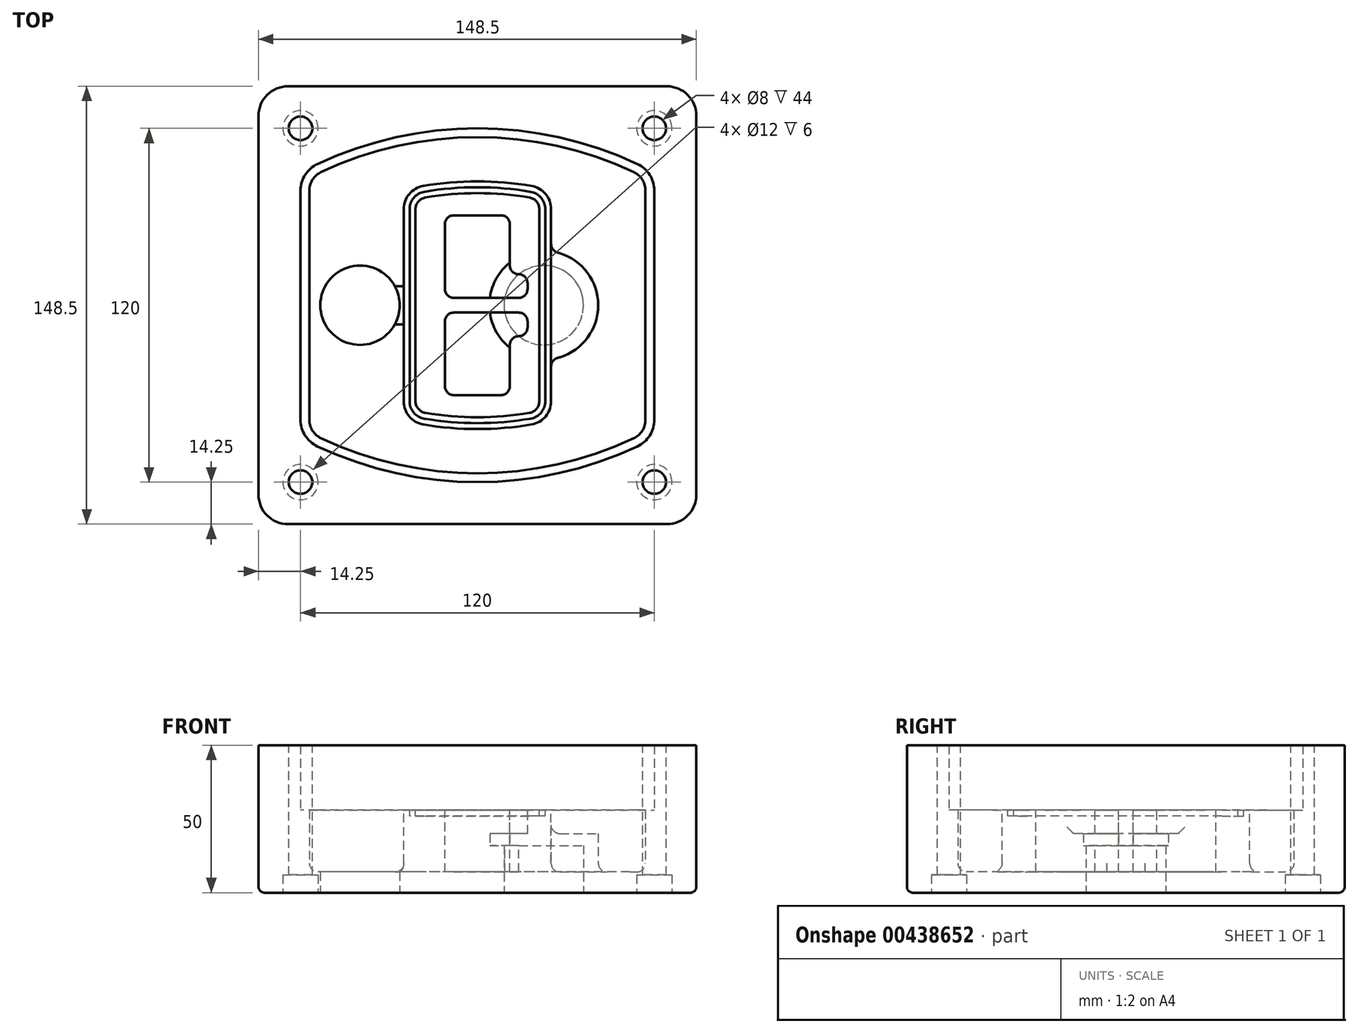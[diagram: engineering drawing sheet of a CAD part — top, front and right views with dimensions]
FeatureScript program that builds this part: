
annotation { "Feature Type Name" : "Feature", "Feature Type Description" : "" }
export const myFeature = defineFeature(function(context is Context, id is Id, definition is map)
    precondition{}
    {
        {
            var Q0;
            Q0=qCreatedBy(makeId("Top.planeOp"),FACE);
            var sketch = newSketch(context, id + "F0", { "sketchPlane" : qUnion([Q0])});
            skPoint(sketch, "E0.rect.middle", {"position": v(0, 0) * mm});
            skLineSegment(sketch, "E1.bottom", {"start": v(-64.25, -74.25) * mm, "end": v(64.25, -74.25) * mm});
            skLineSegment(sketch, "E1.top", {"start": v(-64.25, 74.25) * mm, "end": v(64.25, 74.25) * mm});
            skLineSegment(sketch, "E1.left", {"start": v(-74.25, -64.25) * mm, "end": v(-74.25, 64.25) * mm});
            skLineSegment(sketch, "E1.right", {"start": v(74.25, -64.25) * mm, "end": v(74.25, 64.25) * mm});
            skLineSegment(sketch, "E2", {"start": v(-74.25, 74.25) * mm, "end": v(74.25, -74.25) * mm, "construction": true});
            skLineSegment(sketch, "E3", {"start": v(74.25, 74.25) * mm, "end": v(-74.25, -74.25) * mm, "construction": true});
            skCircle(sketch, "E4", {"center": v(-60, 60) * mm, "radius": 4 * mm});
            skCircle(sketch, "E5", {"center": v(60, 60) * mm, "radius": 4 * mm});
            skCircle(sketch, "E6", {"center": v(60, -60) * mm, "radius": 4 * mm});
            skCircle(sketch, "E7", {"center": v(-60, -60) * mm, "radius": 4 * mm});
            skLineSegment(sketch, "E8", {"start": v(-60, 60) * mm, "end": v(60, 60) * mm, "construction": true});
            skLineSegment(sketch, "E9", {"start": v(60, 60) * mm, "end": v(60, -60) * mm, "construction": true});
            skLineSegment(sketch, "E10", {"start": v(60, -60) * mm, "end": v(-60, -60) * mm, "construction": true});
            skLineSegment(sketch, "E11", {"start": v(-60, -60) * mm, "end": v(-60, 60) * mm, "construction": true});
            skLineSegment(sketch, "E12", {"start": v(-60, 38.83) * mm, "end": v(-60, -38.83) * mm});
            skLineSegment(sketch, "E13", {"start": v(60, 38.83) * mm, "end": v(60, -38.83) * mm});
            skArc(sketch, "E14", {"start": v(54.26, 47.88) * mm, "mid": v(0, 60) * mm, "end": v(-54.26, 47.88) * mm});
            skArc(sketch, "E15", {"start": v(-54.26, -47.88) * mm, "mid": v(0, -60) * mm, "end": v(54.26, -47.88) * mm});
            skLineSegment(sketch, "E16", {"start": v(-60, 0) * mm, "end": v(60, 0) * mm, "construction": true});
            skPoint(sketch, "E17.visualSharp", {"position": v(-60, -45) * mm});
            skArc(sketch, "E17.filletArc", {"start": v(-60, -38.83) * mm, "mid": v(-58.44, -44.2) * mm, "end": v(-54.26, -47.88) * mm});
            skPoint(sketch, "E18.visualSharp", {"position": v(-60, 45) * mm});
            skArc(sketch, "E18.filletArc", {"start": v(-54.26, 47.88) * mm, "mid": v(-58.44, 44.2) * mm, "end": v(-60, 38.83) * mm});
            skPoint(sketch, "E19.visualSharp", {"position": v(60, 45) * mm});
            skArc(sketch, "E19.filletArc", {"start": v(60, 38.83) * mm, "mid": v(58.44, 44.2) * mm, "end": v(54.26, 47.88) * mm});
            skPoint(sketch, "E20.visualSharp", {"position": v(60, -45) * mm});
            skArc(sketch, "E20.filletArc", {"start": v(54.26, -47.88) * mm, "mid": v(58.44, -44.2) * mm, "end": v(60, -38.83) * mm});
            skPoint(sketch, "E21.visualSharp", {"position": v(-74.25, 74.25) * mm});
            skArc(sketch, "E21.filletArc", {"start": v(-64.25, 74.25) * mm, "mid": v(-71.32, 71.32) * mm, "end": v(-74.25, 64.25) * mm});
            skPoint(sketch, "E22.visualSharp", {"position": v(74.25, 74.25) * mm});
            skArc(sketch, "E22.filletArc", {"start": v(74.25, 64.25) * mm, "mid": v(71.32, 71.32) * mm, "end": v(64.25, 74.25) * mm});
            skPoint(sketch, "E23.visualSharp", {"position": v(74.25, -74.25) * mm});
            skArc(sketch, "E23.filletArc", {"start": v(64.25, -74.25) * mm, "mid": v(71.32, -71.32) * mm, "end": v(74.25, -64.25) * mm});
            skPoint(sketch, "E24.visualSharp", {"position": v(-74.25, -74.25) * mm});
            skArc(sketch, "E24.filletArc", {"start": v(-74.25, -64.25) * mm, "mid": v(-71.32, -71.32) * mm, "end": v(-64.25, -74.25) * mm});
            skArc(sketch, "E25.0", {"start": v(57, 38.83) * mm, "mid": v(55.9, 42.58) * mm, "end": v(52.98, 45.17) * mm});
            skLineSegment(sketch, "E25.1", {"start": v(57, 38.83) * mm, "end": v(57, -38.83) * mm});
            skArc(sketch, "E25.2", {"start": v(52.98, -45.17) * mm, "mid": v(55.9, -42.58) * mm, "end": v(57, -38.83) * mm});
            skArc(sketch, "E25.3", {"start": v(-52.98, -45.17) * mm, "mid": v(0, -57) * mm, "end": v(52.98, -45.17) * mm});
            skArc(sketch, "E25.4", {"start": v(-57, -38.83) * mm, "mid": v(-55.9, -42.58) * mm, "end": v(-52.98, -45.17) * mm});
            skArc(sketch, "E25.5", {"start": v(52.98, 45.17) * mm, "mid": v(0, 57) * mm, "end": v(-52.98, 45.17) * mm});
            skLineSegment(sketch, "E25.6", {"start": v(-57, 38.83) * mm, "end": v(-57, -38.83) * mm});
            skArc(sketch, "E25.7", {"start": v(-52.98, 45.17) * mm, "mid": v(-55.9, 42.58) * mm, "end": v(-57, 38.83) * mm});
            skArc(sketch, "E26.0", {"start": v(-55.96, 51.5) * mm, "mid": v(-61.82, 46.33) * mm, "end": v(-64, 38.83) * mm});
            skArc(sketch, "E26.1", {"start": v(55.96, 51.5) * mm, "mid": v(0, 64) * mm, "end": v(-55.96, 51.5) * mm});
            skArc(sketch, "E26.2", {"start": v(64, 38.83) * mm, "mid": v(61.82, 46.33) * mm, "end": v(55.96, 51.5) * mm});
            skLineSegment(sketch, "E26.3", {"start": v(64, 38.83) * mm, "end": v(64, -38.83) * mm});
            skArc(sketch, "E26.4", {"start": v(55.96, -51.5) * mm, "mid": v(61.82, -46.33) * mm, "end": v(64, -38.83) * mm});
            skLineSegment(sketch, "E26.5", {"start": v(-64, 38.83) * mm, "end": v(-64, -38.83) * mm});
            skArc(sketch, "E26.6", {"start": v(-55.96, -51.5) * mm, "mid": v(0, -64) * mm, "end": v(55.96, -51.5) * mm});
            skArc(sketch, "E26.7", {"start": v(-64, -38.83) * mm, "mid": v(-61.82, -46.33) * mm, "end": v(-55.96, -51.5) * mm});
            skSolve(sketch);
        }
        {
            var Q0;
            Q0=makeQuery(id+"F0.imprint","IMPRINT",FACE,{"disambiguationData":[TD([[makeQuery(id+"F0.imprint","IMPRINT",EDGE,{"derivedFrom":sQuery(id+"F0.wireOp",EDGE,"E1.bottom")}),1.0]])]});
            var Q1;
            Q1=makeQuery(id+"F0.imprint","IMPRINT",FACE,{"disambiguationData":[TD([[makeQuery(id+"F0.imprint","IMPRINT",EDGE,{"derivedFrom":sQuery(id+"F0.wireOp",EDGE,"E12")}),1.0]])]});
            var Q2;
            Q2=makeQuery(id+"F0.imprint","IMPRINT",FACE,{"disambiguationData":[TD([[makeQuery(id+"F0.imprint","IMPRINT",EDGE,{"derivedFrom":sQuery(id+"F0.wireOp",EDGE,"E25.0")}),1.0]])]});
            var Q3;
            Q3=makeQuery(id+"F0.imprint","IMPRINT",FACE,{"disambiguationData":[TD([[makeQuery(id+"F0.imprint","IMPRINT",EDGE,{"derivedFrom":sQuery(id+"F0.wireOp",EDGE,"E12")}),-1.0]])]});
            extrude(context, id + "F1", {"entities" : qUnion([Q0, Q1, Q2, Q3]), "oppositeDirection" : true, "depth" : 25 * mm});
        }
        {
            var Q0;
            Q0=makeQuery(id+"F0.imprint","IMPRINT",FACE,{"disambiguationData":[TD([[makeQuery(id+"F0.imprint","IMPRINT",EDGE,{"derivedFrom":sQuery(id+"F0.wireOp",EDGE,"E12")}),1.0]])]});
            extrude(context, id + "F2", {"entities" : qUnion([Q0]), "operationType" : NewBodyOperationType.ADD, "depth" : 3 * mm});
        }
        {
            var Q0;
            Q0=makeQuery(id+"F0.imprint","IMPRINT",FACE,{"disambiguationData":[TD([[makeQuery(id+"F0.imprint","IMPRINT",EDGE,{"derivedFrom":sQuery(id+"F0.wireOp",EDGE,"E25.0")}),1.0]])]});
            extrude(context, id + "F3", {"entities" : qUnion([Q0]), "operationType" : NewBodyOperationType.REMOVE, "oppositeDirection" : true, "depth" : 18 * mm});
        }
        {
            var Q0;
            Q0=makeQuery(id+"F2.opExtrude","CAP_FACE",FACE,{"disambiguationData":[OSD([sQuery(id+"F0.wireOp",EDGE,"E12"),sQuery(id+"F0.wireOp",EDGE,"E13"),sQuery(id+"F0.wireOp",EDGE,"E14"),sQuery(id+"F0.wireOp",EDGE,"E15"),sQuery(id+"F0.wireOp",EDGE,"E17.filletArc"),sQuery(id+"F0.wireOp",EDGE,"E18.filletArc"),sQuery(id+"F0.wireOp",EDGE,"E19.filletArc"),sQuery(id+"F0.wireOp",EDGE,"E20.filletArc"),sQuery(id+"F0.wireOp",EDGE,"E25.0"),sQuery(id+"F0.wireOp",EDGE,"E25.1"),sQuery(id+"F0.wireOp",EDGE,"E25.2"),sQuery(id+"F0.wireOp",EDGE,"E25.3"),sQuery(id+"F0.wireOp",EDGE,"E25.4"),sQuery(id+"F0.wireOp",EDGE,"E25.5"),sQuery(id+"F0.wireOp",EDGE,"E25.6"),sQuery(id+"F0.wireOp",EDGE,"E25.7")])],"isStart":false});
            var sketch = newSketch(context, id + "F4", { "sketchPlane" : qUnion([Q0])});
            skArc(sketch, "E27.0", {"start": v(-18.34, -40.45) * mm, "mid": v(0, -42) * mm, "end": v(18.34, -40.45) * mm});
            skArc(sketch, "E28.0", {"start": v(18.34, 40.45) * mm, "mid": v(0, 42) * mm, "end": v(-18.34, 40.45) * mm});
            skLineSegment(sketch, "E29", {"start": v(-25, 32.57) * mm, "end": v(-25, -32.57) * mm});
            skLineSegment(sketch, "E30", {"start": v(25, 32.57) * mm, "end": v(25, -32.57) * mm});
            skLineSegment(sketch, "E31", {"start": v(-25, 39.1) * mm, "end": v(25, 39.1) * mm, "construction": true});
            skLineSegment(sketch, "E32", {"start": v(-25, -39.1) * mm, "end": v(25, -39.1) * mm, "construction": true});
            skPoint(sketch, "E33.visualSharp", {"position": v(-25, 39.1) * mm});
            skArc(sketch, "E33.filletArc", {"start": v(-18.34, 40.45) * mm, "mid": v(-23.11, 37.73) * mm, "end": v(-25, 32.57) * mm});
            skPoint(sketch, "E34.visualSharp", {"position": v(25, 39.1) * mm});
            skArc(sketch, "E34.filletArc", {"start": v(25, 32.57) * mm, "mid": v(23.11, 37.73) * mm, "end": v(18.34, 40.45) * mm});
            skPoint(sketch, "E35.visualSharp", {"position": v(25, -39.1) * mm});
            skArc(sketch, "E35.filletArc", {"start": v(18.34, -40.45) * mm, "mid": v(23.11, -37.73) * mm, "end": v(25, -32.57) * mm});
            skPoint(sketch, "E36.visualSharp", {"position": v(-25, -39.1) * mm});
            skArc(sketch, "E36.filletArc", {"start": v(-25, -32.57) * mm, "mid": v(-23.11, -37.73) * mm, "end": v(-18.34, -40.45) * mm});
            skArc(sketch, "E37.0", {"start": v(52.98, 45.17) * mm, "mid": v(0, 57) * mm, "end": v(-52.98, 45.17) * mm});
            skArc(sketch, "E37.1", {"start": v(-52.98, 45.17) * mm, "mid": v(-55.9, 42.58) * mm, "end": v(-57, 38.83) * mm});
            skLineSegment(sketch, "E37.2", {"start": v(-57, 38.83) * mm, "end": v(-57, -38.83) * mm});
            skArc(sketch, "E37.3", {"start": v(-57, -38.83) * mm, "mid": v(-55.9, -42.58) * mm, "end": v(-52.98, -45.17) * mm});
            skArc(sketch, "E37.4", {"start": v(-52.98, -45.17) * mm, "mid": v(0, -57) * mm, "end": v(52.98, -45.17) * mm});
            skArc(sketch, "E37.5", {"start": v(52.98, -45.17) * mm, "mid": v(55.9, -42.58) * mm, "end": v(57, -38.83) * mm});
            skLineSegment(sketch, "E37.6", {"start": v(57, 38.83) * mm, "end": v(57, -38.83) * mm});
            skArc(sketch, "E37.7", {"start": v(57, 38.83) * mm, "mid": v(55.9, 42.58) * mm, "end": v(52.98, 45.17) * mm});
            skLineSegment(sketch, "E38.0", {"start": v(23, 32.57) * mm, "end": v(23, -32.57) * mm});
            skArc(sketch, "E38.1", {"start": v(18, -38.48) * mm, "mid": v(21.58, -36.44) * mm, "end": v(23, -32.57) * mm});
            skArc(sketch, "E38.2", {"start": v(-18, -38.48) * mm, "mid": v(0, -40) * mm, "end": v(18, -38.48) * mm});
            skArc(sketch, "E38.3", {"start": v(-23, -32.57) * mm, "mid": v(-21.58, -36.44) * mm, "end": v(-18, -38.48) * mm});
            skLineSegment(sketch, "E38.4", {"start": v(-23, 32.57) * mm, "end": v(-23, -32.57) * mm});
            skArc(sketch, "E38.5", {"start": v(23, 32.57) * mm, "mid": v(21.58, 36.44) * mm, "end": v(18, 38.48) * mm});
            skArc(sketch, "E38.6", {"start": v(-18, 38.48) * mm, "mid": v(-21.58, 36.44) * mm, "end": v(-23, 32.57) * mm});
            skArc(sketch, "E38.7", {"start": v(18, 38.48) * mm, "mid": v(0, 40) * mm, "end": v(-18, 38.48) * mm});
            skArc(sketch, "E39.0", {"start": v(21, 32.57) * mm, "mid": v(20.06, 35.15) * mm, "end": v(17.67, 36.5) * mm});
            skLineSegment(sketch, "E39.1", {"start": v(21, 32.57) * mm, "end": v(21, -32.57) * mm});
            skArc(sketch, "E39.2", {"start": v(17.67, -36.5) * mm, "mid": v(20.06, -35.15) * mm, "end": v(21, -32.57) * mm});
            skArc(sketch, "E39.3", {"start": v(-17.67, -36.5) * mm, "mid": v(0, -38) * mm, "end": v(17.67, -36.5) * mm});
            skArc(sketch, "E39.4", {"start": v(-21, -32.57) * mm, "mid": v(-20.06, -35.15) * mm, "end": v(-17.67, -36.5) * mm});
            skArc(sketch, "E39.5", {"start": v(17.67, 36.5) * mm, "mid": v(0, 38) * mm, "end": v(-17.67, 36.5) * mm});
            skLineSegment(sketch, "E39.6", {"start": v(-21, 32.57) * mm, "end": v(-21, -32.57) * mm});
            skArc(sketch, "E39.7", {"start": v(-17.67, 36.5) * mm, "mid": v(-20.06, 35.15) * mm, "end": v(-21, 32.57) * mm});
            skLineSegment(sketch, "E40", {"start": v(-25, 0) * mm, "end": v(25, 0) * mm, "construction": true});
            skLineSegment(sketch, "E41", {"start": v(-11, 5.5) * mm, "end": v(-11, 27.5) * mm});
            skLineSegment(sketch, "E42", {"start": v(-8, 30.5) * mm, "end": v(8, 30.5) * mm});
            skLineSegment(sketch, "E43", {"start": v(11, 27.5) * mm, "end": v(11, 13.5) * mm});
            skLineSegment(sketch, "E44", {"start": v(14, 10.5) * mm, "end": v(14, 10.5) * mm});
            skLineSegment(sketch, "E45", {"start": v(17, 7.5) * mm, "end": v(17, 5.5) * mm});
            skLineSegment(sketch, "E46", {"start": v(14, 2.5) * mm, "end": v(-8, 2.5) * mm});
            skPoint(sketch, "E47.visualSharp", {"position": v(-11, 30.5) * mm});
            skArc(sketch, "E47.filletArc", {"start": v(-8, 30.5) * mm, "mid": v(-10.12, 29.62) * mm, "end": v(-11, 27.5) * mm});
            skPoint(sketch, "E48.visualSharp", {"position": v(11, 30.5) * mm});
            skArc(sketch, "E48.filletArc", {"start": v(11, 27.5) * mm, "mid": v(10.12, 29.62) * mm, "end": v(8, 30.5) * mm});
            skPoint(sketch, "E49.visualSharp", {"position": v(11, 10.5) * mm});
            skArc(sketch, "E49.filletArc", {"start": v(11, 13.5) * mm, "mid": v(11.88, 11.38) * mm, "end": v(14, 10.5) * mm});
            skPoint(sketch, "E50.visualSharp", {"position": v(17, 10.5) * mm});
            skArc(sketch, "E50.filletArc", {"start": v(17, 7.5) * mm, "mid": v(16.12, 9.62) * mm, "end": v(14, 10.5) * mm});
            skPoint(sketch, "E51.visualSharp", {"position": v(17, 2.5) * mm});
            skArc(sketch, "E51.filletArc", {"start": v(14, 2.5) * mm, "mid": v(16.12, 3.38) * mm, "end": v(17, 5.5) * mm});
            skPoint(sketch, "E52.visualSharp", {"position": v(-11, 2.5) * mm});
            skArc(sketch, "E52.filletArc", {"start": v(-11, 5.5) * mm, "mid": v(-10.12, 3.38) * mm, "end": v(-8, 2.5) * mm});
            skLineSegment(sketch, "E53.0.MirrorCS", {"start": v(14, -2.5) * mm, "end": v(-8, -2.5) * mm});
            skArc(sketch, "E54.0.MirrorCS", {"start": v(-11, -5.5) * mm, "mid": v(-10.12, -3.38) * mm, "end": v(-8, -2.5) * mm});
            skLineSegment(sketch, "E55.0.MirrorCS", {"start": v(-11, -5.5) * mm, "end": v(-11, -27.5) * mm});
            skArc(sketch, "E56.0.MirrorCS", {"start": v(-8, -30.5) * mm, "mid": v(-10.12, -29.62) * mm, "end": v(-11, -27.5) * mm});
            skLineSegment(sketch, "E57.0.MirrorCS", {"start": v(-8, -30.5) * mm, "end": v(8, -30.5) * mm});
            skArc(sketch, "E58.0.MirrorCS", {"start": v(11, -27.5) * mm, "mid": v(10.12, -29.62) * mm, "end": v(8, -30.5) * mm});
            skLineSegment(sketch, "E59.0.MirrorCS", {"start": v(11, -27.5) * mm, "end": v(11, -13.5) * mm});
            skArc(sketch, "E60.0.MirrorCS", {"start": v(11, -13.5) * mm, "mid": v(11.88, -11.38) * mm, "end": v(14, -10.5) * mm});
            skArc(sketch, "E61.0.MirrorCS", {"start": v(17, -7.5) * mm, "mid": v(16.12, -9.62) * mm, "end": v(14, -10.5) * mm});
            skLineSegment(sketch, "E62.0.MirrorCS", {"start": v(17, -7.5) * mm, "end": v(17, -5.5) * mm});
            skArc(sketch, "E63.0.MirrorCS", {"start": v(14, -2.5) * mm, "mid": v(16.12, -3.38) * mm, "end": v(17, -5.5) * mm});
            skSolve(sketch);
        }
        {
            var Q0;
            Q0=makeQuery(id+"F4.imprint","IMPRINT",FACE,{"disambiguationData":[TD([[makeQuery(id+"F4.imprint","IMPRINT",EDGE,{"derivedFrom":sQuery(id+"F4.wireOp",EDGE,"E27.0")}),1.0]])]});
            var Q1;
            Q1=makeQuery(id+"F4.imprint","IMPRINT",FACE,{"disambiguationData":[TD([[makeQuery(id+"F4.imprint","IMPRINT",EDGE,{"derivedFrom":sQuery(id+"F4.wireOp",EDGE,"E38.0")}),-1.0]])]});
            var Q2;
            Q2=makeQuery(id+"F4.imprint","IMPRINT",FACE,{"disambiguationData":[TD([[makeQuery(id+"F4.imprint","IMPRINT",EDGE,{"derivedFrom":sQuery(id+"F4.wireOp",EDGE,"E39.0")}),1.0]])]});
            extrude(context, id + "F5", {"entities" : qUnion([Q0, Q1, Q2]), "operationType" : NewBodyOperationType.ADD, "endBound" : BoundingType.UP_TO_NEXT, "oppositeDirection" : true, "depth" : 25 * mm});
        }
        {
            var Q0;
            Q0=makeQuery(id+"F4.imprint","IMPRINT",FACE,{"disambiguationData":[TD([[makeQuery(id+"F4.imprint","IMPRINT",EDGE,{"derivedFrom":sQuery(id+"F4.wireOp",EDGE,"E38.0")}),-1.0]])]});
            extrude(context, id + "F6", {"entities" : qUnion([Q0]), "operationType" : NewBodyOperationType.REMOVE, "oppositeDirection" : true, "depth" : 2 * mm});
        }
        {
            var Q0;
            Q0=makeQuery(id+"F1.opExtrude","CAP_FACE",FACE,{"disambiguationData":[OSD([sQuery(id+"F0.wireOp",EDGE,"E1.bottom"),sQuery(id+"F0.wireOp",EDGE,"E1.top"),sQuery(id+"F0.wireOp",EDGE,"E1.left"),sQuery(id+"F0.wireOp",EDGE,"E1.right"),sQuery(id+"F0.wireOp",EDGE,"E4"),sQuery(id+"F0.wireOp",EDGE,"E5"),sQuery(id+"F0.wireOp",EDGE,"E6"),sQuery(id+"F0.wireOp",EDGE,"E7"),sQuery(id+"F0.wireOp",EDGE,"E21.filletArc"),sQuery(id+"F0.wireOp",EDGE,"E22.filletArc"),sQuery(id+"F0.wireOp",EDGE,"E23.filletArc"),sQuery(id+"F0.wireOp",EDGE,"E24.filletArc")])],"isStart":false});
            var sketch = newSketch(context, id + "F7", { "sketchPlane" : qUnion([Q0])});
            skCircle(sketch, "E64", {"center": v(22.5, 0) * mm, "radius": 13.47 * mm});
            skCircle(sketch, "E65", {"center": v(-39.81, 0) * mm, "radius": 13.47 * mm});
            skLineSegment(sketch, "E66", {"start": v(74.25, 0) * mm, "end": v(-74.25, 0) * mm});
            skCircle(sketch, "E67", {"center": v(22.5, 0) * mm, "radius": 18.47 * mm});
            skCircle(sketch, "E68", {"center": v(60, -60) * mm, "radius": 6 * mm});
            skCircle(sketch, "E69", {"center": v(-60, -60) * mm, "radius": 6 * mm});
            skCircle(sketch, "E70", {"center": v(-60, 60) * mm, "radius": 6 * mm});
            skCircle(sketch, "E71", {"center": v(60, 60) * mm, "radius": 6 * mm});
            skSolve(sketch);
        }
        {
            var Q0;
            {var subQ1=sQuery(id+"F7.wireOp",EDGE,"E66");var subQ4=sQuery(id+"F7.wireOp",EDGE,"E64");var subQ6=makeQuery(id+"F7.imprint","INTERSECT",VERTEX,{"disambiguationData":[OD(0.0)],"derivedFrom":[subQ4,subQ1]});Q0=makeQuery(id+"F7.imprint","IMPRINT",FACE,{"disambiguationData":[TD([[makeQuery(id+"F7.imprint","IMPRINT",EDGE,{"disambiguationData":[TD([[subQ6,-1.0]])],"derivedFrom":subQ4}),-1.0]])]});}
            var Q1;
            {var subQ0=sQuery(id+"F7.wireOp",EDGE,"E66");var subQ1=sQuery(id+"F7.wireOp",EDGE,"E64");var subQ3=makeQuery(id+"F7.imprint","INTERSECT",VERTEX,{"disambiguationData":[OD(0.0)],"derivedFrom":[subQ1,subQ0]});Q1=makeQuery(id+"F7.imprint","IMPRINT",FACE,{"disambiguationData":[TD([[makeQuery(id+"F7.imprint","IMPRINT",EDGE,{"disambiguationData":[TD([[subQ3,-1.0]])],"derivedFrom":subQ1}),1.0]])]});}
            var Q2;
            {var subQ0=sQuery(id+"F7.wireOp",EDGE,"E66");var subQ1=sQuery(id+"F7.wireOp",EDGE,"E64");var subQ3=makeQuery(id+"F7.imprint","INTERSECT",VERTEX,{"disambiguationData":[OD(0.0)],"derivedFrom":[subQ1,subQ0]});Q2=makeQuery(id+"F7.imprint","IMPRINT",FACE,{"disambiguationData":[TD([[makeQuery(id+"F7.imprint","IMPRINT",EDGE,{"disambiguationData":[TD([[subQ3,1.0]])],"derivedFrom":subQ1}),1.0]])]});}
            var Q3;
            {var subQ1=sQuery(id+"F7.wireOp",EDGE,"E66");var subQ4=sQuery(id+"F7.wireOp",EDGE,"E64");var subQ6=makeQuery(id+"F7.imprint","INTERSECT",VERTEX,{"disambiguationData":[OD(0.0)],"derivedFrom":[subQ4,subQ1]});Q3=makeQuery(id+"F7.imprint","IMPRINT",FACE,{"disambiguationData":[TD([[makeQuery(id+"F7.imprint","IMPRINT",EDGE,{"disambiguationData":[TD([[subQ6,1.0]])],"derivedFrom":subQ4}),-1.0]])]});}
            extrude(context, id + "F8", {"entities" : qUnion([Q0, Q1, Q2, Q3]), "operationType" : NewBodyOperationType.ADD, "oppositeDirection" : true, "depth" : 20 * mm});
        }
        {
            var Q0;
            {var subQ0=sQuery(id+"F7.wireOp",EDGE,"E66");var subQ1=sQuery(id+"F7.wireOp",EDGE,"E64");var subQ3=makeQuery(id+"F7.imprint","INTERSECT",VERTEX,{"disambiguationData":[OD(0.0)],"derivedFrom":[subQ1,subQ0]});Q0=makeQuery(id+"F7.imprint","IMPRINT",FACE,{"disambiguationData":[TD([[makeQuery(id+"F7.imprint","IMPRINT",EDGE,{"disambiguationData":[TD([[subQ3,-1.0]])],"derivedFrom":subQ1}),1.0]])]});}
            var Q1;
            {var subQ0=sQuery(id+"F7.wireOp",EDGE,"E66");var subQ1=sQuery(id+"F7.wireOp",EDGE,"E64");var subQ3=makeQuery(id+"F7.imprint","INTERSECT",VERTEX,{"disambiguationData":[OD(0.0)],"derivedFrom":[subQ1,subQ0]});Q1=makeQuery(id+"F7.imprint","IMPRINT",FACE,{"disambiguationData":[TD([[makeQuery(id+"F7.imprint","IMPRINT",EDGE,{"disambiguationData":[TD([[subQ3,1.0]])],"derivedFrom":subQ1}),1.0]])]});}
            extrude(context, id + "F9", {"entities" : qUnion([Q0, Q1]), "operationType" : NewBodyOperationType.REMOVE, "oppositeDirection" : true, "depth" : 16 * mm});
        }
        {
            var Q0;
            {var subQ0=sQuery(id+"F7.wireOp",EDGE,"E66");var subQ1=sQuery(id+"F7.wireOp",EDGE,"E65");var subQ3=makeQuery(id+"F7.imprint","INTERSECT",VERTEX,{"disambiguationData":[OD(0.0)],"derivedFrom":[subQ1,subQ0]});Q0=makeQuery(id+"F7.imprint","IMPRINT",FACE,{"disambiguationData":[TD([[makeQuery(id+"F7.imprint","IMPRINT",EDGE,{"disambiguationData":[TD([[subQ3,-1.0]])],"derivedFrom":subQ1}),1.0]])]});}
            var Q1;
            {var subQ0=sQuery(id+"F7.wireOp",EDGE,"E66");var subQ1=sQuery(id+"F7.wireOp",EDGE,"E65");var subQ3=makeQuery(id+"F7.imprint","INTERSECT",VERTEX,{"disambiguationData":[OD(0.0)],"derivedFrom":[subQ1,subQ0]});Q1=makeQuery(id+"F7.imprint","IMPRINT",FACE,{"disambiguationData":[TD([[makeQuery(id+"F7.imprint","IMPRINT",EDGE,{"disambiguationData":[TD([[subQ3,1.0]])],"derivedFrom":subQ1}),1.0]])]});}
            extrude(context, id + "F10", {"entities" : qUnion([Q0, Q1]), "operationType" : NewBodyOperationType.REMOVE, "oppositeDirection" : true, "depth" : 25 * mm});
        }
        {
            var Q0;
            Q0=makeQuery(id+"F7.imprint","IMPRINT",FACE,{"disambiguationData":[TD([[makeQuery(id+"F7.imprint","IMPRINT",EDGE,{"derivedFrom":sQuery(id+"F7.wireOp",EDGE,"E68")}),1.0]])]});
            var Q1;
            Q1=makeQuery(id+"F7.imprint","IMPRINT",FACE,{"disambiguationData":[TD([[makeQuery(id+"F7.imprint","IMPRINT",EDGE,{"derivedFrom":makeQuery(id+"F1.opExtrude","CAP_EDGE",EDGE,{"disambiguationData":[OSD([sQuery(id+"F0.wireOp",EDGE,"E5")])],"isStart":false})}),-1.0]])]});
            var Q2;
            Q2=makeQuery(id+"F7.imprint","IMPRINT",FACE,{"disambiguationData":[TD([[makeQuery(id+"F7.imprint","IMPRINT",EDGE,{"derivedFrom":sQuery(id+"F7.wireOp",EDGE,"E69")}),1.0]])]});
            var Q3;
            Q3=makeQuery(id+"F7.imprint","IMPRINT",FACE,{"disambiguationData":[TD([[makeQuery(id+"F7.imprint","IMPRINT",EDGE,{"derivedFrom":makeQuery(id+"F1.opExtrude","CAP_EDGE",EDGE,{"disambiguationData":[OSD([sQuery(id+"F0.wireOp",EDGE,"E4")])],"isStart":false})}),-1.0]])]});
            var Q4;
            Q4=makeQuery(id+"F7.imprint","IMPRINT",FACE,{"disambiguationData":[TD([[makeQuery(id+"F7.imprint","IMPRINT",EDGE,{"derivedFrom":sQuery(id+"F7.wireOp",EDGE,"E70")}),1.0]])]});
            var Q5;
            Q5=makeQuery(id+"F7.imprint","IMPRINT",FACE,{"disambiguationData":[TD([[makeQuery(id+"F7.imprint","IMPRINT",EDGE,{"derivedFrom":makeQuery(id+"F1.opExtrude","CAP_EDGE",EDGE,{"disambiguationData":[OSD([sQuery(id+"F0.wireOp",EDGE,"E7")])],"isStart":false})}),-1.0]])]});
            var Q6;
            Q6=makeQuery(id+"F7.imprint","IMPRINT",FACE,{"disambiguationData":[TD([[makeQuery(id+"F7.imprint","IMPRINT",EDGE,{"derivedFrom":sQuery(id+"F7.wireOp",EDGE,"E71")}),1.0]])]});
            var Q7;
            Q7=makeQuery(id+"F7.imprint","IMPRINT",FACE,{"disambiguationData":[TD([[makeQuery(id+"F7.imprint","IMPRINT",EDGE,{"derivedFrom":makeQuery(id+"F1.opExtrude","CAP_EDGE",EDGE,{"disambiguationData":[OSD([sQuery(id+"F0.wireOp",EDGE,"E6")])],"isStart":false})}),-1.0]])]});
            extrude(context, id + "F11", {"entities" : qUnion([Q0, Q1, Q2, Q3, Q4, Q5, Q6, Q7]), "operationType" : NewBodyOperationType.REMOVE, "oppositeDirection" : true, "depth" : 6 * mm});
        }
        {
            var Q0;
            Q0=makeQuery(id+"F9.boolean.opBoolean","COPY",FACE,{"derivedFrom":makeQuery(id+"F9.opExtrude","CAP_FACE",FACE,{"disambiguationData":[OSD([sQuery(id+"F7.wireOp",EDGE,"E64")])],"isStart":false})});
            var sketch = newSketch(context, id + "F12", { "sketchPlane" : qUnion([Q0])});
            skArc(sketch, "E72.0", {"start": v(11, 14.45) * mm, "mid": v(6.45, 9.13) * mm, "end": v(4.2, 2.5) * mm});
            skArc(sketch, "E72.1", {"start": v(4.2, -2.5) * mm, "mid": v(6.45, -9.13) * mm, "end": v(11, -14.45) * mm});
            skLineSegment(sketch, "E73", {"start": v(4.2, -2.5) * mm, "end": v(14, -2.5) * mm});
            skLineSegment(sketch, "E74.0", {"start": v(14, 2.5) * mm, "end": v(4.2, 2.5) * mm});
            skArc(sketch, "E74.1", {"start": v(14, 2.5) * mm, "mid": v(16.12, 3.38) * mm, "end": v(17, 5.5) * mm});
            skLineSegment(sketch, "E74.2", {"start": v(17, 7.5) * mm, "end": v(17, 5.5) * mm});
            skArc(sketch, "E74.3", {"start": v(17, 7.5) * mm, "mid": v(16.12, 9.62) * mm, "end": v(14, 10.5) * mm});
            skArc(sketch, "E74.4", {"start": v(11, 13.5) * mm, "mid": v(11.88, 11.38) * mm, "end": v(14, 10.5) * mm});
            skLineSegment(sketch, "E74.5", {"start": v(11, 14.45) * mm, "end": v(11, 13.5) * mm});
            skLineSegment(sketch, "E74.7", {"start": v(14, -2.5) * mm, "end": v(4.2, -2.5) * mm});
            skArc(sketch, "E74.8", {"start": v(14, -2.5) * mm, "mid": v(16.12, -3.38) * mm, "end": v(17, -5.5) * mm});
            skLineSegment(sketch, "E74.9", {"start": v(17, -7.5) * mm, "end": v(17, -5.5) * mm});
            skArc(sketch, "E74.10", {"start": v(17, -7.5) * mm, "mid": v(16.12, -9.62) * mm, "end": v(14, -10.5) * mm});
            skArc(sketch, "E74.11", {"start": v(11, -13.5) * mm, "mid": v(11.88, -11.38) * mm, "end": v(14, -10.5) * mm});
            skLineSegment(sketch, "E74.12", {"start": v(11, -14.45) * mm, "end": v(11, -13.5) * mm});
            skPoint(sketch, "E75.orphan", {"position": v(11, -27.5) * mm});
            skPoint(sketch, "E76.orphan", {"position": v(-8, -2.5) * mm});
            skPoint(sketch, "E77.orphan", {"position": v(-8, 2.5) * mm});
            skPoint(sketch, "E78.orphan", {"position": v(11, 27.5) * mm});
            skSolve(sketch);
        }
        {
            var Q0;
            {var subQ7=sQuery(id+"F12.wireOp",EDGE,"E72.0");var subQ14=sQuery(id+"F12.wireOp",EDGE,"E72.1");var subQ16=sQuery(id+"F12.wireOp",EDGE,"E74.1");var subQ18=sQuery(id+"F12.wireOp",EDGE,"E74.8");Q0=qUnion([makeQuery(id+"F12.imprint","IMPRINT",FACE,{"disambiguationData":[TD([[makeQuery(id+"F12.imprint","IMPRINT",EDGE,{"derivedFrom":subQ7}),1.0]])]}),makeQuery(id+"F12.imprint","IMPRINT",FACE,{"disambiguationData":[TD([[makeQuery(id+"F12.imprint","IMPRINT",EDGE,{"derivedFrom":subQ14}),1.0]])]}),makeQuery(id+"F12.imprint","IMPRINT",FACE,{"disambiguationData":[TD([[makeQuery(id+"F12.imprint","IMPRINT",EDGE,{"derivedFrom":subQ16}),1.0]])]}),makeQuery(id+"F12.imprint","IMPRINT",FACE,{"disambiguationData":[TD([[makeQuery(id+"F12.imprint","IMPRINT",EDGE,{"derivedFrom":subQ18}),-1.0]])]})]);}
            var Q1;
            Q1=makeQuery(id+"F5.boolean.opBoolean","SPLIT",FACE,{"disambiguationData":[TD([makeQuery(id+"F5.opExtrude","SWEPT_FACE",FACE,{"disambiguationData":[OSD([sQuery(id+"F4.wireOp",EDGE,"E41")])]})])],"derivedFrom":makeQuery(id+"F3.boolean.opBoolean","COPY",FACE,{"derivedFrom":makeQuery(id+"F3.opExtrude","CAP_FACE",FACE,{"disambiguationData":[OSD([sQuery(id+"F0.wireOp",EDGE,"E25.0"),sQuery(id+"F0.wireOp",EDGE,"E25.1"),sQuery(id+"F0.wireOp",EDGE,"E25.2"),sQuery(id+"F0.wireOp",EDGE,"E25.3"),sQuery(id+"F0.wireOp",EDGE,"E25.4"),sQuery(id+"F0.wireOp",EDGE,"E25.5"),sQuery(id+"F0.wireOp",EDGE,"E25.6"),sQuery(id+"F0.wireOp",EDGE,"E25.7")])],"isStart":false})})});
            extrude(context, id + "F13", {"entities" : qUnion([Q0]), "operationType" : NewBodyOperationType.REMOVE, "endBound" : BoundingType.UP_TO_SURFACE, "endBoundEntityFace" : qUnion([Q1]), "depth" : 25 * mm});
        }
        {
            var Q0;
            Q0=makeQuery(id+"F3.boolean.opBoolean","COPY",EDGE,{"derivedFrom":makeQuery(id+"F3.opExtrude","CAP_EDGE",EDGE,{"disambiguationData":[OSD([sQuery(id+"F0.wireOp",EDGE,"E25.6")])],"isStart":false})});
            var Q1;
            Q1=makeQuery(id+"F8.boolean.opBoolean","INTERSECT",EDGE,{"derivedFrom":[makeQuery(id+"F5.opExtrude","SWEPT_FACE",FACE,{"disambiguationData":[OSD([sQuery(id+"F4.wireOp",EDGE,"E30")])]}),makeQuery(id+"F8.opExtrude","CAP_FACE",FACE,{"disambiguationData":[OSD([sQuery(id+"F7.wireOp",EDGE,"E67")])],"isStart":false})]});
            var Q2;
            Q2=makeQuery(id+"F8.boolean.opBoolean","INTERSECT",EDGE,{"disambiguationData":[OD(1.0)],"derivedFrom":[makeQuery(id+"F5.opExtrude","SWEPT_FACE",FACE,{"disambiguationData":[OSD([sQuery(id+"F4.wireOp",EDGE,"E30")])]}),makeQuery(id+"F8.opExtrude","SWEPT_FACE",FACE,{"disambiguationData":[OSD([sQuery(id+"F7.wireOp",EDGE,"E67")])]})]});
            var Q3;
            {var subQ0=sQuery(id+"F4.wireOp",EDGE,"E30");Q3=makeQuery(id+"F8.boolean.opBoolean","SPLIT",EDGE,{"disambiguationData":[TD([makeQuery(id+"F5.opExtrude","SWEPT_FACE",FACE,{"disambiguationData":[OSD([sQuery(id+"F4.wireOp",EDGE,"E35.filletArc")])]})])],"derivedFrom":makeQuery(id+"F5.opExtrude","CAP_EDGE",EDGE,{"disambiguationData":[OSD([subQ0])],"isStart":false})});}
            var Q4;
            {var subQ0=sQuery(id+"F0.wireOp",EDGE,"E25.7");var subQ1=sQuery(id+"F0.wireOp",EDGE,"E25.1");var subQ2=sQuery(id+"F0.wireOp",EDGE,"E25.6");var subQ3=sQuery(id+"F0.wireOp",EDGE,"E25.5");var subQ4=sQuery(id+"F0.wireOp",EDGE,"E25.4");var subQ5=sQuery(id+"F0.wireOp",EDGE,"E25.0");var subQ6=sQuery(id+"F0.wireOp",EDGE,"E25.2");var subQ7=sQuery(id+"F0.wireOp",EDGE,"E25.3");Q4=makeQuery(id+"F8.boolean.opBoolean","INTERSECT",EDGE,{"derivedFrom":[makeQuery(id+"F5.boolean.opBoolean","SPLIT",FACE,{"disambiguationData":[TD([makeQuery(id+"F2.opExtrude","SWEPT_FACE",FACE,{"disambiguationData":[OSD([subQ5])]})])],"derivedFrom":makeQuery(id+"F3.boolean.opBoolean","COPY",FACE,{"derivedFrom":makeQuery(id+"F3.opExtrude","CAP_FACE",FACE,{"disambiguationData":[OSD([subQ5,subQ1,subQ6,subQ7,subQ4,subQ3,subQ2,subQ0])],"isStart":false})})}),makeQuery(id+"F8.opExtrude","SWEPT_FACE",FACE,{"disambiguationData":[OSD([sQuery(id+"F7.wireOp",EDGE,"E67")])]})]});}
            var Q5;
            Q5=makeQuery(id+"F8.boolean.opBoolean","INTERSECT",EDGE,{"disambiguationData":[OD(0.0)],"derivedFrom":[makeQuery(id+"F5.opExtrude","SWEPT_FACE",FACE,{"disambiguationData":[OSD([sQuery(id+"F4.wireOp",EDGE,"E30")])]}),makeQuery(id+"F8.opExtrude","SWEPT_FACE",FACE,{"disambiguationData":[OSD([sQuery(id+"F7.wireOp",EDGE,"E67")])]})]});
            fillet(context, id + "F14", {"entities" : qUnion([Q0, Q1, Q2, Q3, Q4, Q5]), "radius" : 3 * mm, "tangentPropagation" : true, "allowEdgeOverflow" : false});
        }
        {
            var Q0;
            Q0=makeQuery(id+"F1.opExtrude","CAP_EDGE",EDGE,{"disambiguationData":[OSD([sQuery(id+"F0.wireOp",EDGE,"E1.bottom")])],"isStart":false});
            fillet(context, id + "F15", {"entities" : qUnion([Q0]), "radius" : 2 * mm, "tangentPropagation" : true, "allowEdgeOverflow" : false});
        }
        {
            var Q0;
            {var subQ0=sQuery(id+"F0.wireOp",EDGE,"E21.filletArc");var subQ1=sQuery(id+"F0.wireOp",EDGE,"E7");var subQ2=sQuery(id+"F0.wireOp",EDGE,"E6");var subQ3=sQuery(id+"F0.wireOp",EDGE,"E5");var subQ4=sQuery(id+"F0.wireOp",EDGE,"E4");var subQ5=sQuery(id+"F0.wireOp",EDGE,"E22.filletArc");var subQ6=sQuery(id+"F0.wireOp",EDGE,"E1.bottom");var subQ7=sQuery(id+"F0.wireOp",EDGE,"E1.right");var subQ8=sQuery(id+"F0.wireOp",EDGE,"E1.top");var subQ9=sQuery(id+"F0.wireOp",EDGE,"E1.left");var subQ10=sQuery(id+"F0.wireOp",EDGE,"E23.filletArc");var subQ11=sQuery(id+"F0.wireOp",EDGE,"E24.filletArc");Q0=makeQuery(id+"F2.boolean.opBoolean","SPLIT",FACE,{"disambiguationData":[TD([makeQuery(id+"F1.opExtrude","SWEPT_FACE",FACE,{"disambiguationData":[OSD([subQ6])]})])],"derivedFrom":makeQuery(id+"F1.opExtrude","CAP_FACE",FACE,{"disambiguationData":[OSD([subQ6,subQ8,subQ9,subQ7,subQ4,subQ3,subQ2,subQ1,subQ0,subQ5,subQ10,subQ11])],"isStart":true})});}
            extrude(context, id + "F16", {"entities" : qUnion([Q0]), "operationType" : NewBodyOperationType.ADD, "depth" : 25 * mm});
        }
    });
